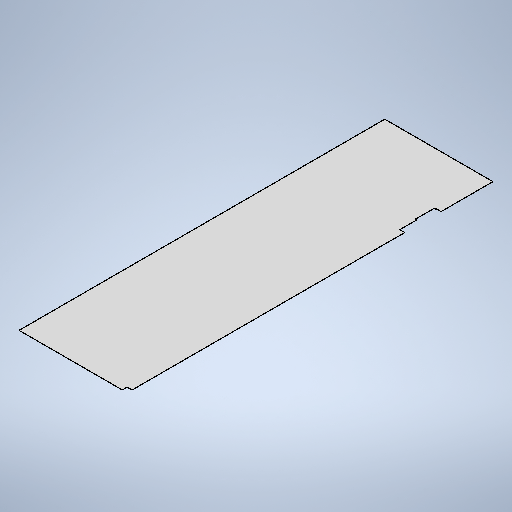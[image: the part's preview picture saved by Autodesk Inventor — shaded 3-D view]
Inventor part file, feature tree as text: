
AUTODESK INVENTOR PART (.ipt)
format: ipt  version: 2025.1 (Build 291241020, 241B)  size: 303,616 bytes
history: native  units: mm
features: other x2, sheet_metal_op x1, chamfer x1, sketch x1
ambient origin geometry x8: Origin, YZ Plane, XZ Plane, XY Plane, X Axis, Y Axis, Z Axis, Center Point
bodies: Body1 (feature_tree)
feature tree (5):
  sheet_metal_op  "Face3"
  chamfer  "Corner Round1"
  sketch  "Sketch1"  dims[d61=500.0mm d154=865.0mm d155=2925.0mm d156=2.0mm d157=40.0mm d158=15.0mm d159=290.0mm d161=40.0mm d162=2220.0mm d163=10.0mm d164=150.0mm d165=5.0mm]
  other  "Plate5"
  other  "Definition1"
